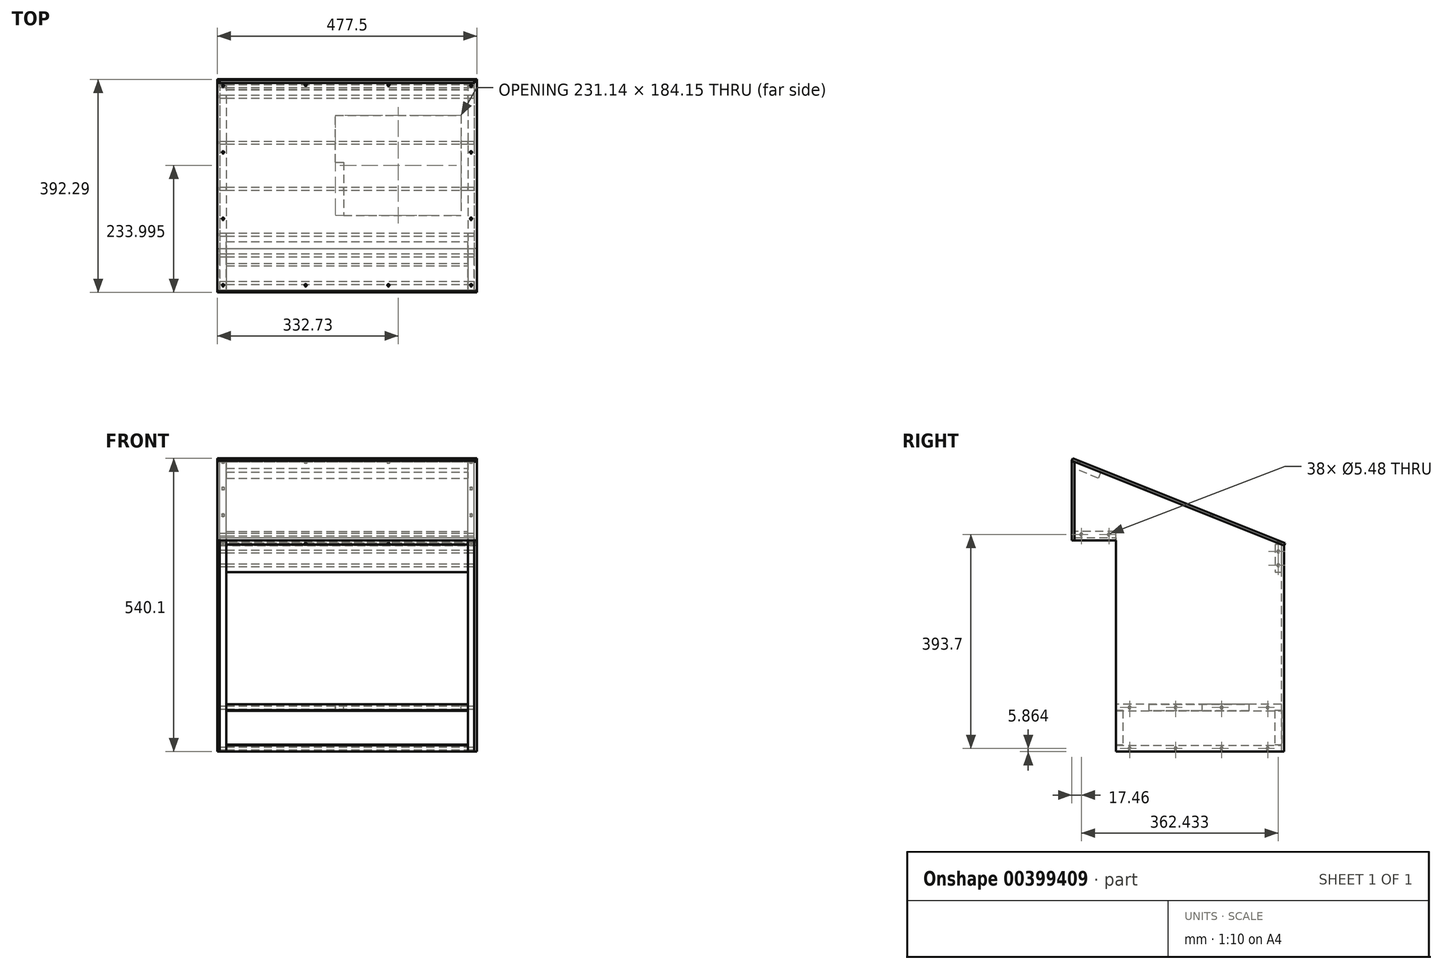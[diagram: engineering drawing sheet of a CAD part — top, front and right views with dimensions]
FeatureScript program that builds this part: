
annotation { "Feature Type Name" : "Feature", "Feature Type Description" : "" }
export const myFeature = defineFeature(function(context is Context, id is Id, definition is map)
    precondition{}
    {
        {
            var Q0;
            Q0=qCreatedBy(makeId("Right.planeOp"),FACE);
            var sketch = newSketch(context, id + "F0", { "sketchPlane" : qUnion([Q0])});
            skLineSegment(sketch, "E0", {"start": v(381, -307.97) * mm, "end": v(381, 73.03) * mm});
            skLineSegment(sketch, "E1", {"start": v(381, 73.03) * mm, "end": v(0, 225.8) * mm});
            skLineSegment(sketch, "E2", {"start": v(0, 85.73) * mm, "end": v(76.2, 85.73) * mm});
            skLineSegment(sketch, "E3", {"start": v(76.2, 85.73) * mm, "end": v(76.2, -307.97) * mm});
            skLineSegment(sketch, "E4", {"start": v(0, 85.73) * mm, "end": v(0, 225.8) * mm});
            skLineSegment(sketch, "E5", {"start": v(381, -221) * mm, "end": v(76.2, -221) * mm});
            skLineSegment(sketch, "E6", {"start": v(381, -307.97) * mm, "end": v(76.2, -307.97) * mm});
            skLineSegment(sketch, "E7", {"start": v(76.2, -296.24) * mm, "end": v(381, -296.24) * mm});
            skLineSegment(sketch, "E8", {"start": v(76.2, -232.74) * mm, "end": v(381, -232.74) * mm});
            skLineSegment(sketch, "E9", {"start": v(76.2, 85.73) * mm, "end": v(76.2, 97.46) * mm});
            skLineSegment(sketch, "E10", {"start": v(76.2, 97.46) * mm, "end": v(0, 97.46) * mm});
            skLineSegment(sketch, "E11", {"start": v(381, 73.03) * mm, "end": v(369.27, 73.03) * mm});
            skLineSegment(sketch, "E12", {"start": v(369.27, 73.03) * mm, "end": v(369.27, 22.23) * mm});
            skLineSegment(sketch, "E13", {"start": v(369.27, 22.23) * mm, "end": v(381, 22.23) * mm});
            skLineSegment(sketch, "E14", {"start": v(0, 225.8) * mm, "end": v(-4.76, 227.71) * mm});
            skLineSegment(sketch, "E15", {"start": v(-4.76, 227.71) * mm, "end": v(-4.76, 225.8) * mm});
            skLineSegment(sketch, "E16", {"start": v(-4.76, 225.8) * mm, "end": v(0, 225.8) * mm});
            skLineSegment(sketch, "E17", {"start": v(-4.76, 225.8) * mm, "end": v(-4.76, 85.73) * mm});
            skLineSegment(sketch, "E18", {"start": v(-4.76, 85.73) * mm, "end": v(0, 85.73) * mm});
            skLineSegment(sketch, "E19", {"start": v(-4.76, 85.73) * mm, "end": v(-4.76, 80.96) * mm});
            skLineSegment(sketch, "E20", {"start": v(-4.76, 80.96) * mm, "end": v(0, 80.96) * mm});
            skLineSegment(sketch, "E21", {"start": v(0, 80.96) * mm, "end": v(0, 85.73) * mm});
            skLineSegment(sketch, "E22", {"start": v(381, 73.03) * mm, "end": v(381, 78.6) * mm});
            skLineSegment(sketch, "E23", {"start": v(381, 78.6) * mm, "end": v(385.6, 78.6) * mm});
            skCircle(sketch, "E24", {"center": v(101.6, -302.1) * mm, "radius": 2.74 * mm});
            skCircle(sketch, "E25", {"center": v(355.6, -302.1) * mm, "radius": 2.74 * mm});
            skCircle(sketch, "E26", {"center": v(186.26, -302.1) * mm, "radius": 2.74 * mm});
            skCircle(sketch, "E27", {"center": v(270.94, -302.1) * mm, "radius": 2.74 * mm});
            skCircle(sketch, "E28.0.1.0", {"center": v(101.6, -226.87) * mm, "radius": 2.74 * mm});
            skCircle(sketch, "E28.0.1.1", {"center": v(186.26, -226.87) * mm, "radius": 2.74 * mm});
            skCircle(sketch, "E28.0.1.2", {"center": v(270.94, -226.87) * mm, "radius": 2.74 * mm});
            skCircle(sketch, "E28.0.1.3", {"center": v(355.6, -226.87) * mm, "radius": 2.74 * mm});
            skLineSegment(sketch, "E28.direction1", {"start": v(101.6, -302.1) * mm, "end": v(127, -302.1) * mm, "construction": true});
            skLineSegment(sketch, "E28.direction2", {"start": v(101.6, -302.1) * mm, "end": v(101.6, -226.87) * mm, "construction": true});
            skCircle(sketch, "E29", {"center": v(12.7, 91.6) * mm, "radius": 2.74 * mm});
            skCircle(sketch, "E30", {"center": v(63.5, 91.6) * mm, "radius": 2.74 * mm});
            skCircle(sketch, "E31", {"center": v(375.13, 60.33) * mm, "radius": 2.74 * mm});
            skCircle(sketch, "E32", {"center": v(375.13, 34.93) * mm, "radius": 2.74 * mm});
            skLineSegment(sketch, "E33", {"start": v(381, 73.03) * mm, "end": v(385.76, 71.12) * mm});
            skLineSegment(sketch, "E34", {"start": v(385.76, 71.12) * mm, "end": v(385.6, 78.6) * mm});
            skLineSegment(sketch, "E35", {"start": v(0, 80.96) * mm, "end": v(76.2, 80.96) * mm});
            skLineSegment(sketch, "E36", {"start": v(385.76, 71.12) * mm, "end": v(385.76, -307.97) * mm});
            skLineSegment(sketch, "E37", {"start": v(385.76, -307.97) * mm, "end": v(381, -307.97) * mm});
            skSolve(sketch);
        }
        {
            var Q0;
            {var subQ0=sQuery(id+"F0.wireOp",EDGE,"E6");Q0=makeQuery(id+"F0.imprint","IMPRINT",FACE,{"disambiguationData":[TD([[makeQuery(id+"F0.imprint","IMPRINT",EDGE,{"derivedFrom":subQ0}),-1.0]])]});}
            var Q1;
            {var subQ0=sQuery(id+"F0.wireOp",EDGE,"E7");Q1=makeQuery(id+"F0.imprint","IMPRINT",FACE,{"disambiguationData":[TD([[makeQuery(id+"F0.imprint","IMPRINT",EDGE,{"derivedFrom":subQ0}),1.0]])]});}
            var Q2;
            {var subQ0=sQuery(id+"F0.wireOp",EDGE,"E5");Q2=makeQuery(id+"F0.imprint","IMPRINT",FACE,{"disambiguationData":[TD([[makeQuery(id+"F0.imprint","IMPRINT",EDGE,{"derivedFrom":subQ0}),1.0]])]});}
            var Q3;
            {var subQ1=sQuery(id+"F0.wireOp",EDGE,"E1");Q3=makeQuery(id+"F0.imprint","IMPRINT",FACE,{"disambiguationData":[TD([[makeQuery(id+"F0.imprint","IMPRINT",EDGE,{"derivedFrom":subQ1}),1.0]])]});}
            var Q4;
            {var subQ0=sQuery(id+"F0.wireOp",EDGE,"E2");Q4=makeQuery(id+"F0.imprint","IMPRINT",FACE,{"disambiguationData":[TD([[makeQuery(id+"F0.imprint","IMPRINT",EDGE,{"derivedFrom":subQ0}),1.0]])]});}
            var Q5;
            {var subQ0=sQuery(id+"F0.wireOp",EDGE,"E11");Q5=makeQuery(id+"F0.imprint","IMPRINT",FACE,{"disambiguationData":[TD([[makeQuery(id+"F0.imprint","IMPRINT",EDGE,{"derivedFrom":subQ0}),1.0]])]});}
            extrude(context, id + "F1", {"entities" : qUnion([Q0, Q1, Q2, Q3, Q4, Q5]), "oppositeDirection" : true, "depth" : 468.93 * mm, "hasSecondDirection" : true, "secondDirectionOppositeDirection" : true, "secondDirectionDepth" : 457.2 * mm});
        }
        {
            var Q0;
            {var subQ3=sQuery(id+"F0.wireOp",EDGE,"E1");Q0=makeQuery(id+"F0.imprint","IMPRINT",FACE,{"disambiguationData":[TD([[makeQuery(id+"F0.imprint","IMPRINT",EDGE,{"derivedFrom":subQ3}),1.0]])]});}
            var Q1;
            {var subQ5=sQuery(id+"F0.wireOp",EDGE,"E5");Q1=makeQuery(id+"F0.imprint","IMPRINT",FACE,{"disambiguationData":[TD([[makeQuery(id+"F0.imprint","IMPRINT",EDGE,{"derivedFrom":subQ5}),1.0]])]});}
            var Q2;
            {var subQ0=sQuery(id+"F0.wireOp",EDGE,"E7");Q2=makeQuery(id+"F0.imprint","IMPRINT",FACE,{"disambiguationData":[TD([[makeQuery(id+"F0.imprint","IMPRINT",EDGE,{"derivedFrom":subQ0}),1.0]])]});}
            var Q3;
            {var subQ0=sQuery(id+"F0.wireOp",EDGE,"E6");Q3=makeQuery(id+"F0.imprint","IMPRINT",FACE,{"disambiguationData":[TD([[makeQuery(id+"F0.imprint","IMPRINT",EDGE,{"derivedFrom":subQ0}),-1.0]])]});}
            var Q4;
            {var subQ0=sQuery(id+"F0.wireOp",EDGE,"E2");Q4=makeQuery(id+"F0.imprint","IMPRINT",FACE,{"disambiguationData":[TD([[makeQuery(id+"F0.imprint","IMPRINT",EDGE,{"derivedFrom":subQ0}),1.0]])]});}
            var Q5;
            {var subQ0=sQuery(id+"F0.wireOp",EDGE,"E11");Q5=makeQuery(id+"F0.imprint","IMPRINT",FACE,{"disambiguationData":[TD([[makeQuery(id+"F0.imprint","IMPRINT",EDGE,{"derivedFrom":subQ0}),1.0]])]});}
            extrude(context, id + "F2", {"entities" : qUnion([Q0, Q1, Q2, Q3, Q4, Q5]), "oppositeDirection" : true, "depth" : 12.7 * mm, "hasSecondDirection" : true, "secondDirectionOppositeDirection" : true, "secondDirectionDepth" : 0.97 * mm});
        }
        {
            var Q0;
            {var subQ0=sQuery(id+"F0.wireOp",EDGE,"E5");Q0=makeQuery(id+"F0.imprint","IMPRINT",FACE,{"disambiguationData":[TD([[makeQuery(id+"F0.imprint","IMPRINT",EDGE,{"derivedFrom":subQ0}),1.0]])]});}
            var Q1;
            {var subQ0=sQuery(id+"F0.wireOp",EDGE,"E6");Q1=makeQuery(id+"F0.imprint","IMPRINT",FACE,{"disambiguationData":[TD([[makeQuery(id+"F0.imprint","IMPRINT",EDGE,{"derivedFrom":subQ0}),-1.0]])]});}
            var Q2;
            {var subQ0=sQuery(id+"F0.wireOp",EDGE,"E2");Q2=makeQuery(id+"F0.imprint","IMPRINT",FACE,{"disambiguationData":[TD([[makeQuery(id+"F0.imprint","IMPRINT",EDGE,{"derivedFrom":subQ0}),1.0]])]});}
            var Q3;
            {var subQ0=sQuery(id+"F0.wireOp",EDGE,"E11");Q3=makeQuery(id+"F0.imprint","IMPRINT",FACE,{"disambiguationData":[TD([[makeQuery(id+"F0.imprint","IMPRINT",EDGE,{"derivedFrom":subQ0}),1.0]])]});}
            extrude(context, id + "F3", {"entities" : qUnion([Q0, Q1, Q2, Q3]), "oppositeDirection" : true, "depth" : 457.2 * mm, "hasSecondDirection" : true, "secondDirectionOppositeDirection" : true, "secondDirectionDepth" : 12.7 * mm});
        }
        {
            var Q0;
            Q0=makeQuery(id+"F3.opExtrude","SWEPT_FACE",FACE,{"disambiguationData":[OSD([sQuery(id+"F0.wireOp",EDGE,"E6")])]});
            cPlane(context, id + "F4", {"entities" : qUnion([Q0]), "cplaneType" : CPlaneType.OFFSET, "offset" : 12.7 * mm, "oppositeDirection" : true, "width" : 152.4 * mm, "height" : 152.4 * mm});
        }
        {
            var Q0;
            Q0=qCreatedBy(id+"F4.planeOp",FACE);
            var sketch = newSketch(context, id + "F5", { "sketchPlane" : qUnion([Q0])});
            skLineSegment(sketch, "E38.bottom", {"start": v(-457.2, -368.3) * mm, "end": v(-12.7, -368.3) * mm});
            skLineSegment(sketch, "E38.top", {"start": v(-457.2, -381) * mm, "end": v(-12.7, -381) * mm});
            skLineSegment(sketch, "E38.left", {"start": v(-457.2, -368.3) * mm, "end": v(-457.2, -381) * mm});
            skLineSegment(sketch, "E38.right", {"start": v(-12.7, -368.3) * mm, "end": v(-12.7, -381) * mm});
            skLineSegment(sketch, "E39.bottom", {"start": v(-457.2, -76.2) * mm, "end": v(-12.7, -76.2) * mm});
            skLineSegment(sketch, "E39.top", {"start": v(-457.2, -88.9) * mm, "end": v(-12.7, -88.9) * mm});
            skLineSegment(sketch, "E39.left", {"start": v(-457.2, -76.2) * mm, "end": v(-457.2, -88.9) * mm});
            skLineSegment(sketch, "E39.right", {"start": v(-12.7, -76.2) * mm, "end": v(-12.7, -88.9) * mm});
            skSolve(sketch);
        }
        {
            var Q0;
            Q0=makeQuery(id+"F5.imprint","IMPRINT",FACE,{"disambiguationData":[TD([[makeQuery(id+"F5.imprint","IMPRINT",EDGE,{"derivedFrom":sQuery(id+"F5.wireOp",EDGE,"E38.bottom")}),-1.0]])]});
            var Q1;
            Q1=makeQuery(id+"F5.imprint","IMPRINT",FACE,{"disambiguationData":[TD([[makeQuery(id+"F5.imprint","IMPRINT",EDGE,{"derivedFrom":sQuery(id+"F5.wireOp",EDGE,"E39.bottom")}),-1.0]])]});
            extrude(context, id + "F6", {"entities" : qUnion([Q0, Q1]), "oppositeDirection" : true, "depth" : 63.5 * mm});
        }
        {
            var Q0;
            Q0=makeQuery(id+"F1.opExtrude","SWEPT_FACE",FACE,{"disambiguationData":[OSD([sQuery(id+"F0.wireOp",EDGE,"E4")])]});
            cPlane(context, id + "F7", {"entities" : qUnion([Q0]), "cplaneType" : CPlaneType.OFFSET, "offset" : 0 * mm, "width" : 152.4 * mm, "height" : 152.4 * mm});
        }
        {
            var Q0;
            Q0=qCreatedBy(id+"F7.planeOp",FACE);
            var sketch = newSketch(context, id + "F8", { "sketchPlane" : qUnion([Q0])});
            skLineSegment(sketch, "E40.bottom", {"start": v(-468.93, 225.8) * mm, "end": v(0, 225.8) * mm});
            skLineSegment(sketch, "E40.top", {"start": v(-468.93, 80.96) * mm, "end": v(0, 80.96) * mm});
            skLineSegment(sketch, "E40.left", {"start": v(-468.93, 225.8) * mm, "end": v(-468.93, 80.96) * mm});
            skLineSegment(sketch, "E40.right", {"start": v(0, 225.8) * mm, "end": v(0, 80.96) * mm});
            skSolve(sketch);
        }
        {
            var Q0;
            Q0=makeQuery(id+"F1.opExtrude","SWEPT_FACE",FACE,{"disambiguationData":[OSD([sQuery(id+"F0.wireOp",EDGE,"E2")])]});
            cPlane(context, id + "F9", {"entities" : qUnion([Q0]), "cplaneType" : CPlaneType.OFFSET, "offset" : 0 * mm, "width" : 152.4 * mm, "height" : 152.4 * mm});
        }
        {
            var Q0;
            Q0=qCreatedBy(id+"F9.planeOp",FACE);
            var sketch = newSketch(context, id + "F10", { "sketchPlane" : qUnion([Q0])});
            skLineSegment(sketch, "E41.bottom", {"start": v(-468.93, 0) * mm, "end": v(-0.97, 0) * mm});
            skLineSegment(sketch, "E41.top", {"start": v(-468.93, -76.2) * mm, "end": v(-0.97, -76.2) * mm});
            skLineSegment(sketch, "E41.left", {"start": v(-468.93, 0) * mm, "end": v(-468.93, -76.2) * mm});
            skLineSegment(sketch, "E41.right", {"start": v(-0.97, 0) * mm, "end": v(-0.97, -76.2) * mm});
            skSolve(sketch);
        }
        {
            var Q0;
            Q0=makeQuery(id+"F10.imprint","IMPRINT",FACE,{"disambiguationData":[TD([[makeQuery(id+"F10.imprint","IMPRINT",EDGE,{"derivedFrom":sQuery(id+"F10.wireOp",EDGE,"E41.bottom")}),-1.0]])]});
            extrude(context, id + "F11", {"entities" : qUnion([Q0]), "depth" : 4.76 * mm});
        }
        {
            var Q0;
            {var subQ0=sQuery(id+"F0.wireOp",EDGE,"E16");Q0=makeQuery(id+"F0.imprint","IMPRINT",FACE,{"disambiguationData":[TD([[makeQuery(id+"F0.imprint","IMPRINT",EDGE,{"derivedFrom":subQ0}),-1.0]])]});}
            var Q1;
            Q1=makeQuery(id+"F0.imprint","IMPRINT",FACE,{"disambiguationData":[TD([[makeQuery(id+"F0.imprint","IMPRINT",EDGE,{"derivedFrom":sQuery(id+"F0.wireOp",EDGE,"E14")}),1.0]])]});
            var Q2;
            Q2=makeQuery(id+"F0.imprint","IMPRINT",FACE,{"disambiguationData":[TD([[makeQuery(id+"F0.imprint","IMPRINT",EDGE,{"derivedFrom":sQuery(id+"F0.wireOp",EDGE,"E18")}),-1.0]])]});
            extrude(context, id + "F12", {"entities" : qUnion([Q0, Q1, Q2]), "oppositeDirection" : true, "depth" : 473.7 * mm, "hasSecondDirection" : true, "secondDirectionOppositeDirection" : false, "secondDirectionDepth" : 3.8 * mm});
        }
        {
            var Q0;
            Q0=makeQuery(id+"F2.opExtrude","SWEPT_FACE",FACE,{"disambiguationData":[OSD([sQuery(id+"F0.wireOp",EDGE,"E1")])]});
            cPlane(context, id + "F13", {"entities" : qUnion([Q0]), "cplaneType" : CPlaneType.OFFSET, "offset" : 0 * mm, "width" : 152.4 * mm, "height" : 152.4 * mm});
        }
        {
            var Q0;
            Q0=qCreatedBy(id+"F13.planeOp",FACE);
            var sketch = newSketch(context, id + "F14", { "sketchPlane" : qUnion([Q0])});
            skLineSegment(sketch, "E42.bottom", {"start": v(3.8, 331.58) * mm, "end": v(-473.7, 331.58) * mm});
            skLineSegment(sketch, "E42.top", {"start": v(3.8, -89.17) * mm, "end": v(-473.7, -89.17) * mm});
            skLineSegment(sketch, "E42.left", {"start": v(3.8, 331.58) * mm, "end": v(3.8, -89.17) * mm});
            skLineSegment(sketch, "E42.right", {"start": v(-473.7, 331.58) * mm, "end": v(-473.7, -89.17) * mm});
            skCircle(sketch, "E43", {"center": v(-6.83, -76.47) * mm, "radius": 2.02 * mm});
            skCircle(sketch, "E44", {"center": v(-6.83, 318.88) * mm, "radius": 2.02 * mm});
            skCircle(sketch, "E45", {"center": v(-6.83, 187.1) * mm, "radius": 2.02 * mm});
            skCircle(sketch, "E46", {"center": v(-6.83, 55.31) * mm, "radius": 2.02 * mm});
            skCircle(sketch, "E47.1.0.0", {"center": v(-463.12, 318.88) * mm, "radius": 2.02 * mm});
            skCircle(sketch, "E47.1.0.1", {"center": v(-463.12, 187.1) * mm, "radius": 2.02 * mm});
            skCircle(sketch, "E47.1.0.2", {"center": v(-463.12, 55.31) * mm, "radius": 2.02 * mm});
            skCircle(sketch, "E47.1.0.3", {"center": v(-463.12, -76.47) * mm, "radius": 2.02 * mm});
            skLineSegment(sketch, "E47.direction1", {"start": v(-6.83, -76.47) * mm, "end": v(-463.12, -76.47) * mm, "construction": true});
            skCircle(sketch, "E48", {"center": v(-158.93, 320.58) * mm, "radius": 2.02 * mm});
            skCircle(sketch, "E49", {"center": v(-311.02, 320.58) * mm, "radius": 2.02 * mm});
            skCircle(sketch, "E50", {"center": v(-158.98, -76.47) * mm, "radius": 2.02 * mm});
            skCircle(sketch, "E51", {"center": v(-311.17, -76.47) * mm, "radius": 2.02 * mm});
            skSolve(sketch);
        }
        {
            var Q0;
            Q0=makeQuery(id+"F14.imprint","IMPRINT",FACE,{"disambiguationData":[TD([[makeQuery(id+"F14.imprint","IMPRINT",EDGE,{"derivedFrom":sQuery(id+"F14.wireOp",EDGE,"E42.bottom")}),1.0]])]});
            extrude(context, id + "F15", {"entities" : qUnion([Q0]), "depth" : 4.76 * mm});
        }
        {
            var Q0;
            Q0=makeQuery(id+"F2.opExtrude","SWEPT_FACE",FACE,{"disambiguationData":[OSD([sQuery(id+"F0.wireOp",EDGE,"E0")])]});
            cPlane(context, id + "F16", {"entities" : qUnion([Q0]), "cplaneType" : CPlaneType.OFFSET, "offset" : 0 * mm, "width" : 152.4 * mm, "height" : 152.4 * mm});
        }
        {
            var Q0;
            Q0=qCreatedBy(id+"F16.planeOp",FACE);
            var sketch = newSketch(context, id + "F17", { "sketchPlane" : qUnion([Q0])});
            skLineSegment(sketch, "E52.bottom", {"start": v(0.97, -307.97) * mm, "end": v(468.93, -307.97) * mm});
            skLineSegment(sketch, "E52.top", {"start": v(0.97, 73.03) * mm, "end": v(468.93, 73.03) * mm});
            skLineSegment(sketch, "E52.left", {"start": v(0.97, -307.97) * mm, "end": v(0.97, 73.03) * mm});
            skLineSegment(sketch, "E52.right", {"start": v(468.93, -307.97) * mm, "end": v(468.93, 73.03) * mm});
            skSolve(sketch);
        }
        {
            var Q0;
            Q0=makeQuery(id+"F17.imprint","IMPRINT",FACE,{"disambiguationData":[TD([[makeQuery(id+"F17.imprint","IMPRINT",EDGE,{"derivedFrom":sQuery(id+"F17.wireOp",EDGE,"E52.bottom")}),1.0]])]});
            extrude(context, id + "F18", {"entities" : qUnion([Q0]), "depth" : 4.76 * mm});
        }
        {
            var Q0;
            Q0=makeQuery(id+"F3.opExtrude","SWEPT_FACE",FACE,{"disambiguationData":[OSD([sQuery(id+"F0.wireOp",EDGE,"E5")])]});
            cPlane(context, id + "F19", {"entities" : qUnion([Q0]), "cplaneType" : CPlaneType.OFFSET, "offset" : 0 * mm, "width" : 152.4 * mm, "height" : 152.4 * mm});
        }
        {
            var Q0;
            Q0=qCreatedBy(id+"F19.planeOp",FACE);
            var sketch = newSketch(context, id + "F20", { "sketchPlane" : qUnion([Q0])});
            skLineSegment(sketch, "E53.bottom", {"start": v(-25.4, 137.16) * mm, "end": v(-241.3, 137.16) * mm});
            skLineSegment(sketch, "E53.top", {"start": v(-25.4, 321.31) * mm, "end": v(-241.3, 321.31) * mm});
            skLineSegment(sketch, "E53.left", {"start": v(-25.4, 137.16) * mm, "end": v(-25.4, 321.31) * mm});
            skLineSegment(sketch, "E53.right", {"start": v(-241.3, 137.16) * mm, "end": v(-241.3, 321.3) * mm});
            skLineSegment(sketch, "E54.bottom", {"start": v(-241.3, 321.31) * mm, "end": v(-256.54, 321.31) * mm});
            skLineSegment(sketch, "E54.top", {"start": v(-241.3, 234.95) * mm, "end": v(-256.54, 234.95) * mm});
            skLineSegment(sketch, "E54.left", {"start": v(-241.3, 321.31) * mm, "end": v(-241.3, 234.95) * mm});
            skLineSegment(sketch, "E54.right", {"start": v(-256.54, 321.3) * mm, "end": v(-256.54, 234.95) * mm});
            skSolve(sketch);
        }
        {
            var Q0;
            Q0=makeQuery(id+"F20.imprint","IMPRINT",FACE,{"disambiguationData":[TD([[makeQuery(id+"F20.imprint","IMPRINT",EDGE,{"derivedFrom":sQuery(id+"F20.wireOp",EDGE,"E53.bottom")}),-1.0]])]});
            var Q1;
            Q1=makeQuery(id+"F20.imprint","IMPRINT",FACE,{"disambiguationData":[TD([[makeQuery(id+"F20.imprint","IMPRINT",EDGE,{"derivedFrom":sQuery(id+"F20.wireOp",EDGE,"E54.bottom")}),1.0]])]});
            extrude(context, id + "F21", {"entities" : qUnion([Q0, Q1]), "operationType" : NewBodyOperationType.REMOVE, "oppositeDirection" : true, "depth" : 30.73 * mm});
        }
        {
            var Q0;
            Q0=makeQuery(id+"F0.imprint","IMPRINT",FACE,{"disambiguationData":[TD([[makeQuery(id+"F0.imprint","IMPRINT",EDGE,{"derivedFrom":sQuery(id+"F0.wireOp",EDGE,"E22")}),-1.0]])]});
            extrude(context, id + "F22", {"entities" : qUnion([Q0]), "operationType" : NewBodyOperationType.REMOVE, "oppositeDirection" : true, "depth" : 502.41 * mm});
        }
        {
            var Q0;
            Q0=makeQuery(id+"F0.imprint","IMPRINT",FACE,{"disambiguationData":[TD([[makeQuery(id+"F0.imprint","IMPRINT",EDGE,{"derivedFrom":sQuery(id+"F0.wireOp",EDGE,"E14")}),1.0]])]});
            var Q1;
            {var subQ0=sQuery(id+"F0.wireOp",EDGE,"E7");Q1=makeQuery(id+"F0.imprint","IMPRINT",FACE,{"disambiguationData":[TD([[makeQuery(id+"F0.imprint","IMPRINT",EDGE,{"derivedFrom":subQ0}),1.0]])]});}
            var Q2;
            {var subQ1=sQuery(id+"F0.wireOp",EDGE,"E11");Q2=makeQuery(id+"F0.imprint","IMPRINT",FACE,{"disambiguationData":[TD([[makeQuery(id+"F0.imprint","IMPRINT",EDGE,{"derivedFrom":subQ1}),1.0]])]});}
            var Q3;
            {var subQ0=sQuery(id+"F0.wireOp",EDGE,"E2");Q3=makeQuery(id+"F0.imprint","IMPRINT",FACE,{"disambiguationData":[TD([[makeQuery(id+"F0.imprint","IMPRINT",EDGE,{"derivedFrom":subQ0}),-1.0]])]});}
            var Q4;
            {var subQ1=sQuery(id+"F0.wireOp",EDGE,"E6");Q4=makeQuery(id+"F0.imprint","IMPRINT",FACE,{"disambiguationData":[TD([[makeQuery(id+"F0.imprint","IMPRINT",EDGE,{"derivedFrom":subQ1}),-1.0]])]});}
            var Q5;
            {var subQ1=sQuery(id+"F0.wireOp",EDGE,"E1");Q5=makeQuery(id+"F0.imprint","IMPRINT",FACE,{"disambiguationData":[TD([[makeQuery(id+"F0.imprint","IMPRINT",EDGE,{"derivedFrom":subQ1}),1.0]])]});}
            var Q6;
            {var subQ0=sQuery(id+"F0.wireOp",EDGE,"E5");Q6=makeQuery(id+"F0.imprint","IMPRINT",FACE,{"disambiguationData":[TD([[makeQuery(id+"F0.imprint","IMPRINT",EDGE,{"derivedFrom":subQ0}),1.0]])]});}
            var Q7;
            {var subQ2=sQuery(id+"F0.wireOp",EDGE,"E2");Q7=makeQuery(id+"F0.imprint","IMPRINT",FACE,{"disambiguationData":[TD([[makeQuery(id+"F0.imprint","IMPRINT",EDGE,{"derivedFrom":subQ2}),1.0]])]});}
            var Q8;
            Q8=makeQuery(id+"F0.imprint","IMPRINT",FACE,{"disambiguationData":[TD([[makeQuery(id+"F0.imprint","IMPRINT",EDGE,{"derivedFrom":sQuery(id+"F0.wireOp",EDGE,"E29")}),1.0]])]});
            var Q9;
            Q9=makeQuery(id+"F0.imprint","IMPRINT",FACE,{"disambiguationData":[TD([[makeQuery(id+"F0.imprint","IMPRINT",EDGE,{"derivedFrom":sQuery(id+"F0.wireOp",EDGE,"E31")}),1.0]])]});
            var Q10;
            Q10=makeQuery(id+"F0.imprint","IMPRINT",FACE,{"disambiguationData":[TD([[makeQuery(id+"F0.imprint","IMPRINT",EDGE,{"derivedFrom":sQuery(id+"F0.wireOp",EDGE,"E32")}),1.0]])]});
            var Q11;
            Q11=makeQuery(id+"F0.imprint","IMPRINT",FACE,{"disambiguationData":[TD([[makeQuery(id+"F0.imprint","IMPRINT",EDGE,{"derivedFrom":sQuery(id+"F0.wireOp",EDGE,"E26")}),1.0]])]});
            var Q12;
            Q12=makeQuery(id+"F0.imprint","IMPRINT",FACE,{"disambiguationData":[TD([[makeQuery(id+"F0.imprint","IMPRINT",EDGE,{"derivedFrom":sQuery(id+"F0.wireOp",EDGE,"E24")}),1.0]])]});
            var Q13;
            Q13=makeQuery(id+"F0.imprint","IMPRINT",FACE,{"disambiguationData":[TD([[makeQuery(id+"F0.imprint","IMPRINT",EDGE,{"derivedFrom":sQuery(id+"F0.wireOp",EDGE,"E28.0.1.0")}),1.0]])]});
            var Q14;
            Q14=makeQuery(id+"F0.imprint","IMPRINT",FACE,{"disambiguationData":[TD([[makeQuery(id+"F0.imprint","IMPRINT",EDGE,{"derivedFrom":sQuery(id+"F0.wireOp",EDGE,"E28.0.1.1")}),1.0]])]});
            var Q15;
            Q15=makeQuery(id+"F0.imprint","IMPRINT",FACE,{"disambiguationData":[TD([[makeQuery(id+"F0.imprint","IMPRINT",EDGE,{"derivedFrom":sQuery(id+"F0.wireOp",EDGE,"E28.0.1.2")}),1.0]])]});
            var Q16;
            Q16=makeQuery(id+"F0.imprint","IMPRINT",FACE,{"disambiguationData":[TD([[makeQuery(id+"F0.imprint","IMPRINT",EDGE,{"derivedFrom":sQuery(id+"F0.wireOp",EDGE,"E28.0.1.3")}),1.0]])]});
            var Q17;
            Q17=makeQuery(id+"F0.imprint","IMPRINT",FACE,{"disambiguationData":[TD([[makeQuery(id+"F0.imprint","IMPRINT",EDGE,{"derivedFrom":sQuery(id+"F0.wireOp",EDGE,"E25")}),1.0]])]});
            var Q18;
            Q18=makeQuery(id+"F0.imprint","IMPRINT",FACE,{"disambiguationData":[TD([[makeQuery(id+"F0.imprint","IMPRINT",EDGE,{"derivedFrom":sQuery(id+"F0.wireOp",EDGE,"E27")}),1.0]])]});
            var Q19;
            Q19=makeQuery(id+"F0.imprint","IMPRINT",FACE,{"disambiguationData":[TD([[makeQuery(id+"F0.imprint","IMPRINT",EDGE,{"derivedFrom":sQuery(id+"F0.wireOp",EDGE,"E30")}),1.0]])]});
            var Q20;
            {var subQ5=sQuery(id+"F0.wireOp",EDGE,"E33");Q20=makeQuery(id+"F0.imprint","IMPRINT",FACE,{"disambiguationData":[TD([[makeQuery(id+"F0.imprint","IMPRINT",EDGE,{"derivedFrom":subQ5}),-1.0]])]});}
            extrude(context, id + "F23", {"entities" : qUnion([Q0, Q1, Q2, Q3, Q4, Q5, Q6, Q7, Q8, Q9, Q10, Q11, Q12, Q13, Q14, Q15, Q16, Q17, Q18, Q19, Q20]), "depth" : 3.8 * mm, "hasSecondDirection" : true, "secondDirectionOppositeDirection" : true, "secondDirectionDepth" : 0.97 * mm});
        }
        {
            var Q0;
            {var subQ0=sQuery(id+"F0.wireOp",EDGE,"E7");Q0=makeQuery(id+"F0.imprint","IMPRINT",FACE,{"disambiguationData":[TD([[makeQuery(id+"F0.imprint","IMPRINT",EDGE,{"derivedFrom":subQ0}),1.0]])]});}
            var Q1;
            {var subQ0=sQuery(id+"F0.wireOp",EDGE,"E2");Q1=makeQuery(id+"F0.imprint","IMPRINT",FACE,{"disambiguationData":[TD([[makeQuery(id+"F0.imprint","IMPRINT",EDGE,{"derivedFrom":subQ0}),-1.0]])]});}
            var Q2;
            {var subQ1=sQuery(id+"F0.wireOp",EDGE,"E11");Q2=makeQuery(id+"F0.imprint","IMPRINT",FACE,{"disambiguationData":[TD([[makeQuery(id+"F0.imprint","IMPRINT",EDGE,{"derivedFrom":subQ1}),1.0]])]});}
            var Q3;
            {var subQ1=sQuery(id+"F0.wireOp",EDGE,"E6");Q3=makeQuery(id+"F0.imprint","IMPRINT",FACE,{"disambiguationData":[TD([[makeQuery(id+"F0.imprint","IMPRINT",EDGE,{"derivedFrom":subQ1}),-1.0]])]});}
            var Q4;
            {var subQ1=sQuery(id+"F0.wireOp",EDGE,"E1");Q4=makeQuery(id+"F0.imprint","IMPRINT",FACE,{"disambiguationData":[TD([[makeQuery(id+"F0.imprint","IMPRINT",EDGE,{"derivedFrom":subQ1}),1.0]])]});}
            var Q5;
            {var subQ0=sQuery(id+"F0.wireOp",EDGE,"E5");Q5=makeQuery(id+"F0.imprint","IMPRINT",FACE,{"disambiguationData":[TD([[makeQuery(id+"F0.imprint","IMPRINT",EDGE,{"derivedFrom":subQ0}),1.0]])]});}
            var Q6;
            {var subQ2=sQuery(id+"F0.wireOp",EDGE,"E2");Q6=makeQuery(id+"F0.imprint","IMPRINT",FACE,{"disambiguationData":[TD([[makeQuery(id+"F0.imprint","IMPRINT",EDGE,{"derivedFrom":subQ2}),1.0]])]});}
            var Q7;
            Q7=makeQuery(id+"F0.imprint","IMPRINT",FACE,{"disambiguationData":[TD([[makeQuery(id+"F0.imprint","IMPRINT",EDGE,{"derivedFrom":sQuery(id+"F0.wireOp",EDGE,"E29")}),1.0]])]});
            var Q8;
            Q8=makeQuery(id+"F0.imprint","IMPRINT",FACE,{"disambiguationData":[TD([[makeQuery(id+"F0.imprint","IMPRINT",EDGE,{"derivedFrom":sQuery(id+"F0.wireOp",EDGE,"E30")}),1.0]])]});
            var Q9;
            Q9=makeQuery(id+"F0.imprint","IMPRINT",FACE,{"disambiguationData":[TD([[makeQuery(id+"F0.imprint","IMPRINT",EDGE,{"derivedFrom":sQuery(id+"F0.wireOp",EDGE,"E31")}),1.0]])]});
            var Q10;
            Q10=makeQuery(id+"F0.imprint","IMPRINT",FACE,{"disambiguationData":[TD([[makeQuery(id+"F0.imprint","IMPRINT",EDGE,{"derivedFrom":sQuery(id+"F0.wireOp",EDGE,"E32")}),1.0]])]});
            var Q11;
            {var subQ5=sQuery(id+"F0.wireOp",EDGE,"E33");Q11=makeQuery(id+"F0.imprint","IMPRINT",FACE,{"disambiguationData":[TD([[makeQuery(id+"F0.imprint","IMPRINT",EDGE,{"derivedFrom":subQ5}),-1.0]])]});}
            var Q12;
            Q12=makeQuery(id+"F0.imprint","IMPRINT",FACE,{"disambiguationData":[TD([[makeQuery(id+"F0.imprint","IMPRINT",EDGE,{"derivedFrom":sQuery(id+"F0.wireOp",EDGE,"E28.0.1.0")}),1.0]])]});
            var Q13;
            Q13=makeQuery(id+"F0.imprint","IMPRINT",FACE,{"disambiguationData":[TD([[makeQuery(id+"F0.imprint","IMPRINT",EDGE,{"derivedFrom":sQuery(id+"F0.wireOp",EDGE,"E28.0.1.1")}),1.0]])]});
            var Q14;
            Q14=makeQuery(id+"F0.imprint","IMPRINT",FACE,{"disambiguationData":[TD([[makeQuery(id+"F0.imprint","IMPRINT",EDGE,{"derivedFrom":sQuery(id+"F0.wireOp",EDGE,"E26")}),1.0]])]});
            var Q15;
            Q15=makeQuery(id+"F0.imprint","IMPRINT",FACE,{"disambiguationData":[TD([[makeQuery(id+"F0.imprint","IMPRINT",EDGE,{"derivedFrom":sQuery(id+"F0.wireOp",EDGE,"E24")}),1.0]])]});
            var Q16;
            Q16=makeQuery(id+"F0.imprint","IMPRINT",FACE,{"disambiguationData":[TD([[makeQuery(id+"F0.imprint","IMPRINT",EDGE,{"derivedFrom":sQuery(id+"F0.wireOp",EDGE,"E28.0.1.2")}),1.0]])]});
            var Q17;
            Q17=makeQuery(id+"F0.imprint","IMPRINT",FACE,{"disambiguationData":[TD([[makeQuery(id+"F0.imprint","IMPRINT",EDGE,{"derivedFrom":sQuery(id+"F0.wireOp",EDGE,"E28.0.1.3")}),1.0]])]});
            var Q18;
            Q18=makeQuery(id+"F0.imprint","IMPRINT",FACE,{"disambiguationData":[TD([[makeQuery(id+"F0.imprint","IMPRINT",EDGE,{"derivedFrom":sQuery(id+"F0.wireOp",EDGE,"E25")}),1.0]])]});
            var Q19;
            Q19=makeQuery(id+"F0.imprint","IMPRINT",FACE,{"disambiguationData":[TD([[makeQuery(id+"F0.imprint","IMPRINT",EDGE,{"derivedFrom":sQuery(id+"F0.wireOp",EDGE,"E27")}),1.0]])]});
            extrude(context, id + "F24", {"entities" : qUnion([Q0, Q1, Q2, Q3, Q4, Q5, Q6, Q7, Q8, Q9, Q10, Q11, Q12, Q13, Q14, Q15, Q16, Q17, Q18, Q19]), "oppositeDirection" : true, "depth" : 473.7 * mm, "hasSecondDirection" : true, "secondDirectionOppositeDirection" : true, "secondDirectionDepth" : 468.93 * mm});
        }
        {
            var Q0;
            {var subQ1=sQuery(id+"F0.wireOp",EDGE,"E1");Q0=makeQuery(id+"F0.imprint","IMPRINT",FACE,{"disambiguationData":[TD([[makeQuery(id+"F0.imprint","IMPRINT",EDGE,{"derivedFrom":subQ1}),1.0]])]});}
            var sketch = newSketch(context, id + "F25", { "sketchPlane" : qUnion([Q0])});
            skLineSegment(sketch, "E55", {"start": v(0, 225.8) * mm, "end": v(48.68, 206.25) * mm});
            skLineSegment(sketch, "E56", {"start": v(48.68, 206.25) * mm, "end": v(44.3, 195.36) * mm});
            skLineSegment(sketch, "E57", {"start": v(44.3, 195.36) * mm, "end": v(0, 213.16) * mm});
            skLineSegment(sketch, "E58", {"start": v(0, 213.16) * mm, "end": v(0, 225.8) * mm});
            skSolve(sketch);
        }
        {
            var Q0;
            Q0 = qSketchRegion(id + "F25", true);
            extrude(context, id + "F26", {"entities" : qUnion([Q0]), "oppositeDirection" : true, "depth" : 457.2 * mm, "hasSecondDirection" : true, "secondDirectionOppositeDirection" : true, "secondDirectionDepth" : 12.7 * mm});
        }
    });
